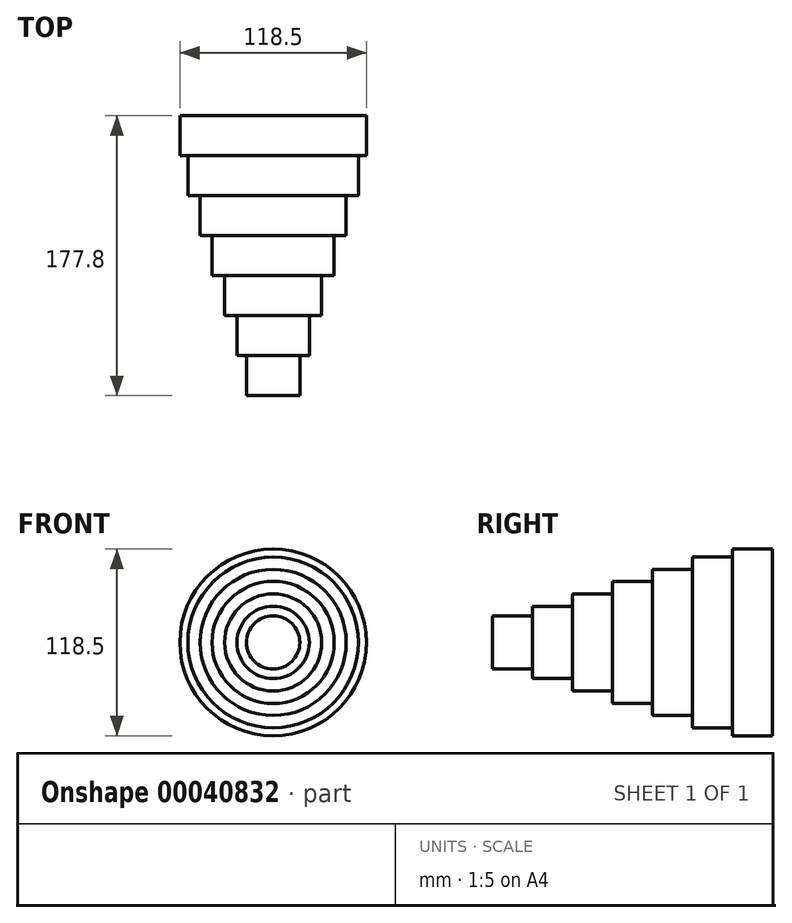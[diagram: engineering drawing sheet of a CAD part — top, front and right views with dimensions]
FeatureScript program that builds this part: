
annotation { "Feature Type Name" : "Feature", "Feature Type Description" : "" }
export const myFeature = defineFeature(function(context is Context, id is Id, definition is map)
    precondition{}
    {
        {
            var Q0;
            Q0=qCreatedBy(makeId("Front.planeOp"),FACE);
            var sketch = newSketch(context, id + "F0", { "sketchPlane" : qUnion([Q0])});
            skCircle(sketch, "E0", {"center": v(0, 0) * mm, "radius": 59.25 * mm});
            skSolve(sketch);
        }
        {
            var Q0;
            Q0=makeQuery(id+"F0.imprint","IMPRINT",FACE,{"disambiguationData":[TD([[makeQuery(id+"F0.imprint","IMPRINT",EDGE,{"derivedFrom":sQuery(id+"F0.wireOp",EDGE,"E0")}),1.0]])]});
            extrude(context, id + "F1", {"entities" : qUnion([Q0]), "depth" : 25.4 * mm});
        }
        {
            var Q0;
            Q0=makeQuery(id+"F1.opExtrude","CAP_FACE",FACE,{"disambiguationData":[OSD([sQuery(id+"F0.wireOp",EDGE,"E0")])],"isStart":false});
            var sketch = newSketch(context, id + "F2", { "sketchPlane" : qUnion([Q0])});
            skCircle(sketch, "E1", {"center": v(0, 0) * mm, "radius": 54.17 * mm});
            skSolve(sketch);
        }
        {
            var Q0;
            Q0=makeQuery(id+"F2.imprint","IMPRINT",FACE,{"disambiguationData":[TD([[makeQuery(id+"F2.imprint","IMPRINT",EDGE,{"derivedFrom":sQuery(id+"F2.wireOp",EDGE,"E1")}),1.0]])]});
            extrude(context, id + "F3", {"entities" : qUnion([Q0]), "operationType" : NewBodyOperationType.ADD, "depth" : 25.4 * mm});
        }
        {
            var Q0;
            Q0=makeQuery(id+"F3.opExtrude","CAP_FACE",FACE,{"disambiguationData":[OSD([sQuery(id+"F2.wireOp",EDGE,"E1")])],"isStart":false});
            var sketch = newSketch(context, id + "F4", { "sketchPlane" : qUnion([Q0])});
            skCircle(sketch, "E2", {"center": v(0, 0) * mm, "radius": 46.4 * mm});
            skSolve(sketch);
        }
        {
            var Q0;
            Q0=makeQuery(id+"F4.imprint","IMPRINT",FACE,{"disambiguationData":[TD([[makeQuery(id+"F4.imprint","IMPRINT",EDGE,{"derivedFrom":sQuery(id+"F4.wireOp",EDGE,"E2")}),1.0]])]});
            extrude(context, id + "F5", {"entities" : qUnion([Q0]), "operationType" : NewBodyOperationType.ADD, "depth" : 25.4 * mm});
        }
        {
            var Q0;
            Q0=makeQuery(id+"F5.opExtrude","CAP_FACE",FACE,{"disambiguationData":[OSD([sQuery(id+"F4.wireOp",EDGE,"E2")])],"isStart":false});
            var sketch = newSketch(context, id + "F6", { "sketchPlane" : qUnion([Q0])});
            skCircle(sketch, "E3", {"center": v(0, 0) * mm, "radius": 38.8 * mm});
            skSolve(sketch);
        }
        {
            var Q0;
            Q0=makeQuery(id+"F6.imprint","IMPRINT",FACE,{"disambiguationData":[TD([[makeQuery(id+"F6.imprint","IMPRINT",EDGE,{"derivedFrom":sQuery(id+"F6.wireOp",EDGE,"E3")}),1.0]])]});
            extrude(context, id + "F7", {"entities" : qUnion([Q0]), "operationType" : NewBodyOperationType.ADD, "depth" : 25.4 * mm});
        }
        {
            var Q0;
            Q0=makeQuery(id+"F7.opExtrude","CAP_FACE",FACE,{"disambiguationData":[OSD([sQuery(id+"F6.wireOp",EDGE,"E3")])],"isStart":false});
            var sketch = newSketch(context, id + "F8", { "sketchPlane" : qUnion([Q0])});
            skCircle(sketch, "E4", {"center": v(0, 0) * mm, "radius": 30.84 * mm});
            skSolve(sketch);
        }
        {
            var Q0;
            Q0=makeQuery(id+"F8.imprint","IMPRINT",FACE,{"disambiguationData":[TD([[makeQuery(id+"F8.imprint","IMPRINT",EDGE,{"derivedFrom":sQuery(id+"F8.wireOp",EDGE,"E4")}),1.0]])]});
            extrude(context, id + "F9", {"entities" : qUnion([Q0]), "operationType" : NewBodyOperationType.ADD, "depth" : 25.4 * mm});
        }
        {
            var Q0;
            Q0=makeQuery(id+"F9.opExtrude","CAP_FACE",FACE,{"disambiguationData":[OSD([sQuery(id+"F8.wireOp",EDGE,"E4")])],"isStart":false});
            var sketch = newSketch(context, id + "F10", { "sketchPlane" : qUnion([Q0])});
            skCircle(sketch, "E5", {"center": v(0, 0) * mm, "radius": 22.98 * mm});
            skSolve(sketch);
        }
        {
            var Q0;
            Q0=makeQuery(id+"F10.imprint","IMPRINT",FACE,{"disambiguationData":[TD([[makeQuery(id+"F10.imprint","IMPRINT",EDGE,{"derivedFrom":sQuery(id+"F10.wireOp",EDGE,"E5")}),1.0]])]});
            extrude(context, id + "F11", {"entities" : qUnion([Q0]), "operationType" : NewBodyOperationType.ADD, "depth" : 25.4 * mm});
        }
        {
            var Q0;
            Q0=makeQuery(id+"F11.opExtrude","CAP_FACE",FACE,{"disambiguationData":[OSD([sQuery(id+"F10.wireOp",EDGE,"E5")])],"isStart":false});
            var sketch = newSketch(context, id + "F12", { "sketchPlane" : qUnion([Q0])});
            skCircle(sketch, "E6", {"center": v(0, 0) * mm, "radius": 16.94 * mm});
            skSolve(sketch);
        }
        {
            var Q0;
            Q0=makeQuery(id+"F12.imprint","IMPRINT",FACE,{"disambiguationData":[TD([[makeQuery(id+"F12.imprint","IMPRINT",EDGE,{"derivedFrom":sQuery(id+"F12.wireOp",EDGE,"E6")}),1.0]])]});
            extrude(context, id + "F13", {"entities" : qUnion([Q0]), "operationType" : NewBodyOperationType.ADD, "depth" : 25.4 * mm});
        }
    });
